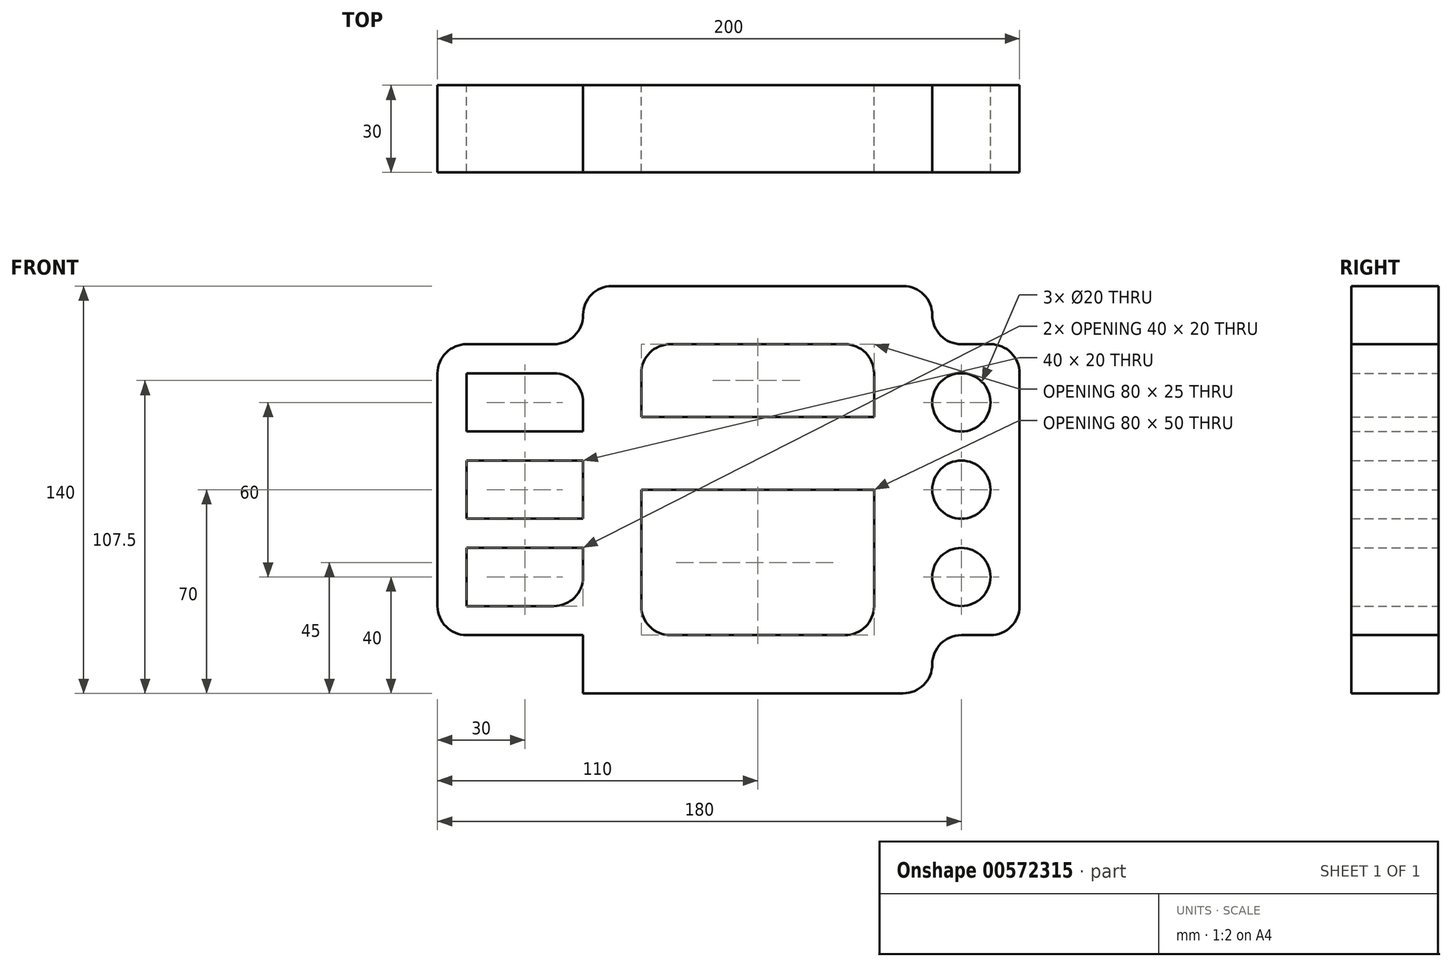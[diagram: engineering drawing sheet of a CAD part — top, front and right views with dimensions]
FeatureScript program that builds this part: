
annotation { "Feature Type Name" : "Feature", "Feature Type Description" : "" }
export const myFeature = defineFeature(function(context is Context, id is Id, definition is map)
    precondition{}
    {
        {
            var Q0;
            Q0=qCreatedBy(makeId("Front.planeOp"),FACE);
            var sketch = newSketch(context, id + "F0", { "sketchPlane" : qUnion([Q0])});
            skLineSegment(sketch, "E0", {"start": v(0, 0) * mm, "end": v(110, 0) * mm});
            skLineSegment(sketch, "E1", {"start": v(120, 10) * mm, "end": v(120, 10) * mm});
            skLineSegment(sketch, "E2", {"start": v(130, 20) * mm, "end": v(140, 20) * mm});
            skLineSegment(sketch, "E3", {"start": v(150, 30) * mm, "end": v(150, 110) * mm});
            skLineSegment(sketch, "E4", {"start": v(140, 120) * mm, "end": v(130, 120) * mm});
            skLineSegment(sketch, "E5", {"start": v(120, 130) * mm, "end": v(120, 130) * mm});
            skLineSegment(sketch, "E6", {"start": v(110, 140) * mm, "end": v(10, 140) * mm});
            skLineSegment(sketch, "E7", {"start": v(0, 130) * mm, "end": v(0, 130) * mm});
            skLineSegment(sketch, "E8", {"start": v(-10, 120) * mm, "end": v(-40, 120) * mm});
            skLineSegment(sketch, "E9", {"start": v(-50, 110) * mm, "end": v(-50, 30) * mm});
            skLineSegment(sketch, "E10", {"start": v(-40, 20) * mm, "end": v(0, 20) * mm});
            skLineSegment(sketch, "E11", {"start": v(0, 20) * mm, "end": v(0, 0) * mm});
            skLineSegment(sketch, "E12.bottom", {"start": v(20, 95) * mm, "end": v(100, 95) * mm});
            skLineSegment(sketch, "E12.top", {"start": v(30, 120) * mm, "end": v(90, 120) * mm});
            skLineSegment(sketch, "E12.left", {"start": v(20, 95) * mm, "end": v(20, 110) * mm});
            skLineSegment(sketch, "E12.right", {"start": v(100, 95) * mm, "end": v(100, 110) * mm});
            skLineSegment(sketch, "E13.bottom", {"start": v(20, 70) * mm, "end": v(100, 70) * mm});
            skLineSegment(sketch, "E13.top", {"start": v(30, 20) * mm, "end": v(90, 20) * mm});
            skLineSegment(sketch, "E13.left", {"start": v(20, 70) * mm, "end": v(20, 30) * mm});
            skLineSegment(sketch, "E13.right", {"start": v(100, 70) * mm, "end": v(100, 30) * mm});
            skLineSegment(sketch, "E14.bottom", {"start": v(-40, 110) * mm, "end": v(-10, 110) * mm});
            skLineSegment(sketch, "E14.top", {"start": v(-40, 90) * mm, "end": v(0, 90) * mm});
            skLineSegment(sketch, "E14.left", {"start": v(-40, 110) * mm, "end": v(-40, 90) * mm});
            skLineSegment(sketch, "E14.right", {"start": v(0, 100) * mm, "end": v(0, 90) * mm});
            skLineSegment(sketch, "E15.bottom", {"start": v(-40, 80) * mm, "end": v(0, 80) * mm});
            skLineSegment(sketch, "E15.top", {"start": v(-40, 60) * mm, "end": v(0, 60) * mm});
            skLineSegment(sketch, "E15.left", {"start": v(-40, 80) * mm, "end": v(-40, 60) * mm});
            skLineSegment(sketch, "E15.right", {"start": v(0, 80) * mm, "end": v(0, 60) * mm});
            skLineSegment(sketch, "E16.bottom", {"start": v(-40, 50) * mm, "end": v(0, 50) * mm});
            skLineSegment(sketch, "E16.top", {"start": v(-40, 30) * mm, "end": v(-10, 30) * mm});
            skLineSegment(sketch, "E16.left", {"start": v(-40, 50) * mm, "end": v(-40, 30) * mm});
            skLineSegment(sketch, "E16.right", {"start": v(0, 50) * mm, "end": v(0, 40) * mm});
            skCircle(sketch, "E17", {"center": v(130, 100) * mm, "radius": 10 * mm});
            skCircle(sketch, "E18", {"center": v(130, 70) * mm, "radius": 10 * mm});
            skCircle(sketch, "E19", {"center": v(130, 40) * mm, "radius": 10 * mm});
            skLineSegment(sketch, "E20", {"start": v(60, 0) * mm, "end": v(60, 20) * mm, "construction": true});
            skPoint(sketch, "E21.visualSharp", {"position": v(120, 20) * mm});
            skArc(sketch, "E21.filletArc", {"start": v(130, 20) * mm, "mid": v(122.93, 17.07) * mm, "end": v(120, 10) * mm});
            skPoint(sketch, "E22.visualSharp", {"position": v(120, 0) * mm});
            skArc(sketch, "E22.filletArc", {"start": v(110, 0) * mm, "mid": v(117.07, 2.93) * mm, "end": v(120, 10) * mm});
            skPoint(sketch, "E23.visualSharp", {"position": v(150, 20) * mm});
            skArc(sketch, "E23.filletArc", {"start": v(140, 20) * mm, "mid": v(147.07, 22.93) * mm, "end": v(150, 30) * mm});
            skPoint(sketch, "E24.visualSharp", {"position": v(150, 120) * mm});
            skArc(sketch, "E24.filletArc", {"start": v(150, 110) * mm, "mid": v(147.07, 117.07) * mm, "end": v(140, 120) * mm});
            skPoint(sketch, "E25.visualSharp", {"position": v(120, 120) * mm});
            skArc(sketch, "E25.filletArc", {"start": v(120, 130) * mm, "mid": v(122.93, 122.93) * mm, "end": v(130, 120) * mm});
            skPoint(sketch, "E26.visualSharp", {"position": v(120, 140) * mm});
            skArc(sketch, "E26.filletArc", {"start": v(120, 130) * mm, "mid": v(117.07, 137.07) * mm, "end": v(110, 140) * mm});
            skPoint(sketch, "E27.visualSharp", {"position": v(0, 140) * mm});
            skArc(sketch, "E27.filletArc", {"start": v(10, 140) * mm, "mid": v(2.93, 137.07) * mm, "end": v(0, 130) * mm});
            skPoint(sketch, "E28.visualSharp", {"position": v(0, 120) * mm});
            skArc(sketch, "E28.filletArc", {"start": v(-10, 120) * mm, "mid": v(-2.93, 122.93) * mm, "end": v(0, 130) * mm});
            skPoint(sketch, "E29.visualSharp", {"position": v(-50, 120) * mm});
            skArc(sketch, "E29.filletArc", {"start": v(-40, 120) * mm, "mid": v(-47.07, 117.07) * mm, "end": v(-50, 110) * mm});
            skPoint(sketch, "E30.visualSharp", {"position": v(-50, 20) * mm});
            skArc(sketch, "E30.filletArc", {"start": v(-50, 30) * mm, "mid": v(-47.07, 22.93) * mm, "end": v(-40, 20) * mm});
            skPoint(sketch, "E31.visualSharp", {"position": v(20, 120) * mm});
            skArc(sketch, "E31.filletArc", {"start": v(30, 120) * mm, "mid": v(22.93, 117.07) * mm, "end": v(20, 110) * mm});
            skPoint(sketch, "E32.visualSharp", {"position": v(100, 120) * mm});
            skArc(sketch, "E32.filletArc", {"start": v(100, 110) * mm, "mid": v(97.07, 117.07) * mm, "end": v(90, 120) * mm});
            skPoint(sketch, "E33.visualSharp", {"position": v(20, 20) * mm});
            skArc(sketch, "E33.filletArc", {"start": v(20, 30) * mm, "mid": v(22.93, 22.93) * mm, "end": v(30, 20) * mm});
            skPoint(sketch, "E34.visualSharp", {"position": v(100, 20) * mm});
            skArc(sketch, "E34.filletArc", {"start": v(90, 20) * mm, "mid": v(97.07, 22.93) * mm, "end": v(100, 30) * mm});
            skPoint(sketch, "E35.visualSharp", {"position": v(0, 30) * mm});
            skArc(sketch, "E35.filletArc", {"start": v(-10, 30) * mm, "mid": v(-2.93, 32.93) * mm, "end": v(0, 40) * mm});
            skPoint(sketch, "E36.visualSharp", {"position": v(0, 110) * mm});
            skArc(sketch, "E36.filletArc", {"start": v(0, 100) * mm, "mid": v(-2.93, 107.07) * mm, "end": v(-10, 110) * mm});
            skSolve(sketch);
        }
        {
            var Q0;
            Q0=qSketchRegion(id+"F0",true);
            extrude(context, id + "F1", {"entities" : qUnion([Q0]), "depth" : 30 * mm, "offsetDistance" : 25 * mm});
        }
    });
